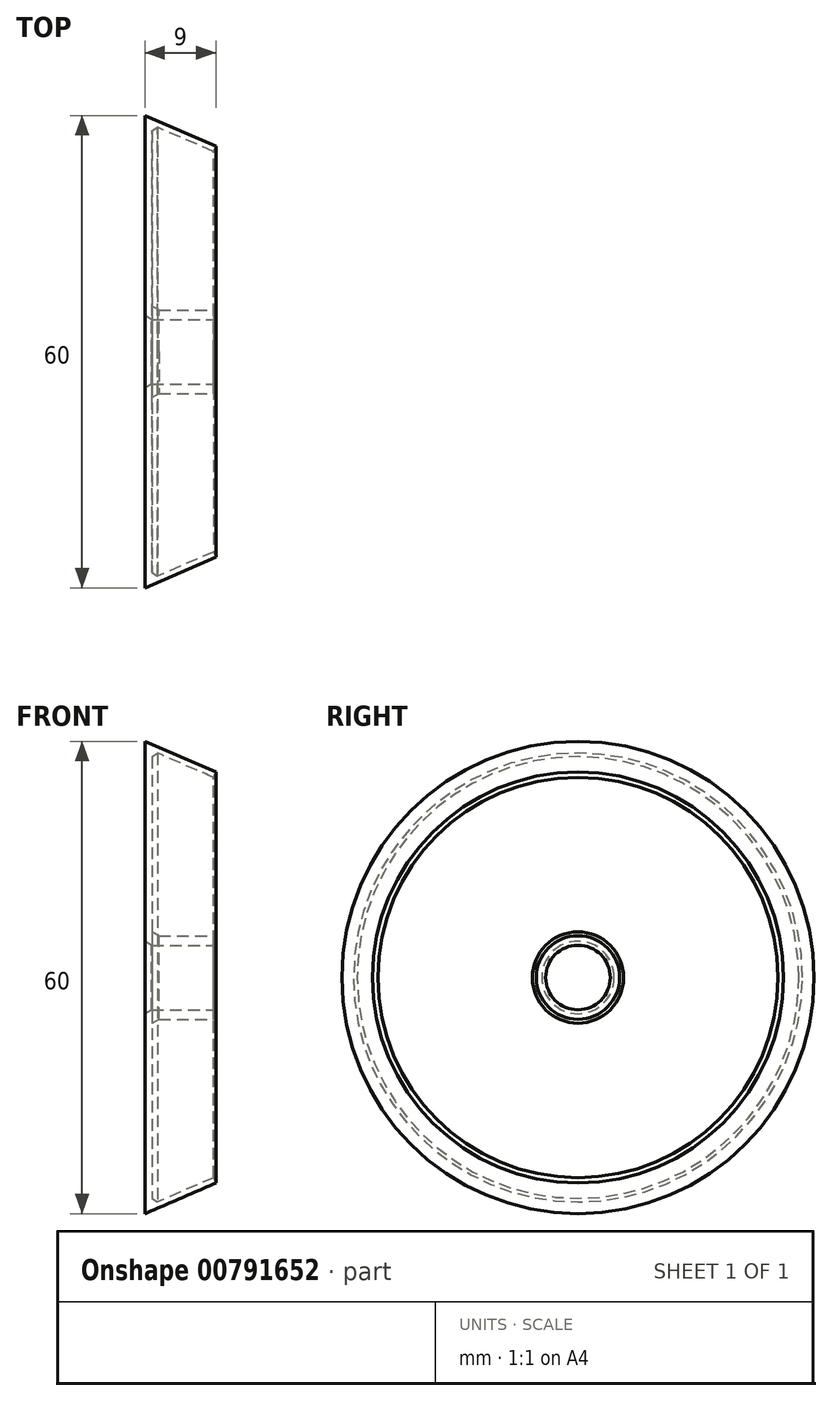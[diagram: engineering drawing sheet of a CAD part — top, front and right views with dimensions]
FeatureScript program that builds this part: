
annotation { "Feature Type Name" : "Feature", "Feature Type Description" : "" }
export const myFeature = defineFeature(function(context is Context, id is Id, definition is map)
    precondition{}
    {
        {
            var Q0;
            Q0=qCreatedBy(makeId("Front.planeOp"),FACE);
            var sketch = newSketch(context, id + "F0", { "sketchPlane" : qUnion([Q0])});
            skLineSegment(sketch, "E0", {"start": v(8.7, 4.1) * mm, "end": v(0, 4.1) * mm});
            skLineSegment(sketch, "E1", {"start": v(0, 4.1) * mm, "end": v(0, 30) * mm});
            skLineSegment(sketch, "E2", {"start": v(0, 30) * mm, "end": v(9, 26.1) * mm});
            skLineSegment(sketch, "E3", {"start": v(9, 26.1) * mm, "end": v(8.7, 25.43) * mm});
            skLineSegment(sketch, "E4", {"start": v(8.7, 25.43) * mm, "end": v(0.9, 28.8) * mm});
            skLineSegment(sketch, "E5", {"start": v(0.9, 28.8) * mm, "end": v(0.9, 5.3) * mm});
            skLineSegment(sketch, "E6", {"start": v(0.9, 5.3) * mm, "end": v(8.7, 5.3) * mm});
            skLineSegment(sketch, "E7", {"start": v(8.7, 5.3) * mm, "end": v(8.7, 4.1) * mm});
            skLineSegment(sketch, "E8", {"start": v(17.9, 0) * mm, "end": v(-11.74, 0) * mm, "construction": true});
            skLineSegment(sketch, "E9", {"start": v(3, 28.7) * mm, "end": v(3, 0) * mm, "construction": true});
            skLineSegment(sketch, "E10", {"start": v(6, 27.4) * mm, "end": v(6, 0) * mm, "construction": true});
            skLineSegment(sketch, "E11", {"start": v(8.7, 25.43) * mm, "end": v(0, 25.43) * mm, "construction": true});
            skLineSegment(sketch, "E12", {"start": v(8.7, 25.43) * mm, "end": v(8.7, 26.23) * mm, "construction": true});
            skSolve(sketch);
        }
        {
            var Q0;
            Q0 = qSketchRegion(id + "F0", true);
            var Q1;
            Q1=sQuery(id+"F0.wireOp",EDGE,"E8");
            revolve(context, id + "F1", {"surfaceOperationType" : NewSurfaceOperationType.NEW, "entities" : qUnion([Q0]), "axis" : qUnion([Q1]), "revolveType" : RevolveType.FULL});
        }
        {
            var Q0;
            Q0=makeQuery(id+"F1.opRevolve","SWEPT_EDGE",EDGE,{"disambiguationData":[OSD([sQuery(id+"F0.wireOp",EDGE,"E0"),sQuery(id+"F0.wireOp",EDGE,"E1")])]});
            chamfer(context, id + "F2", {"entities" : qUnion([Q0]), "chamferType" : ChamferType.OFFSET_ANGLE, "width" : 0.5 * mm, "oppositeDirection" : false, "angle" : 60 * degree});
        }
        {
            var Q0;
            Q0=makeQuery(id+"F1.opRevolve","SWEPT_EDGE",EDGE,{"disambiguationData":[OSD([sQuery(id+"F0.wireOp",EDGE,"E5"),sQuery(id+"F0.wireOp",EDGE,"E6")])]});
            chamfer(context, id + "F3", {"entities" : qUnion([Q0]), "chamferType" : ChamferType.OFFSET_ANGLE, "width" : 0.5 * mm, "oppositeDirection" : true, "angle" : 60 * degree, "tangentPropagation" : true});
        }
        {
            var Q0;
            Q0=makeQuery(id+"F1.opRevolve","SWEPT_EDGE",EDGE,{"disambiguationData":[OSD([sQuery(id+"F0.wireOp",EDGE,"E4"),sQuery(id+"F0.wireOp",EDGE,"E5")])]});
            chamfer(context, id + "F4", {"entities" : qUnion([Q0]), "width" : 0.5 * mm, "tangentPropagation" : true});
        }
    });
